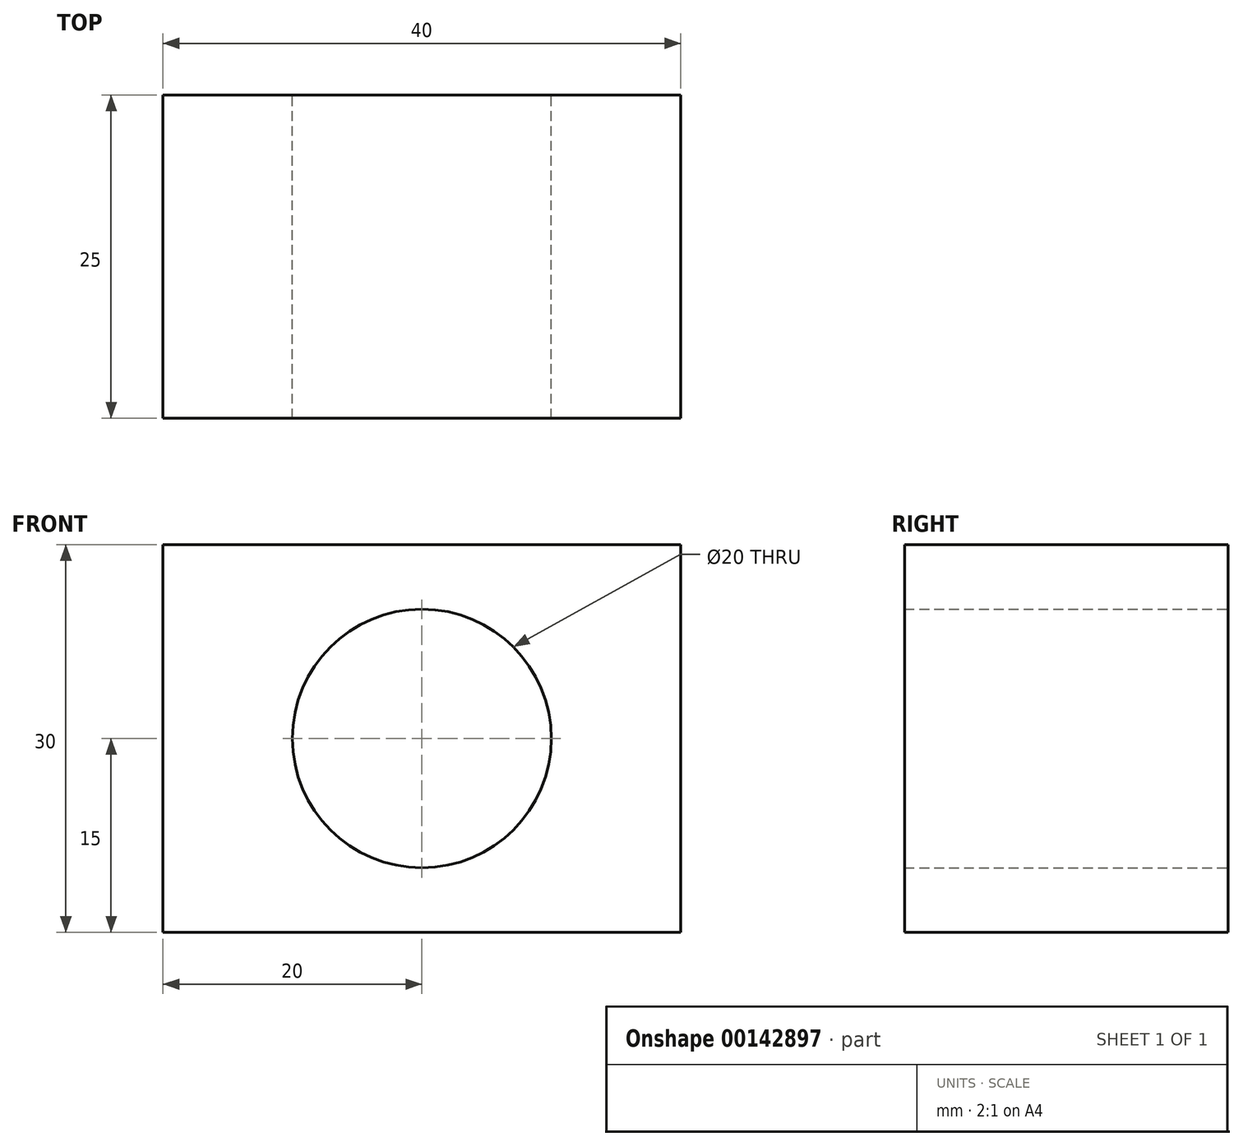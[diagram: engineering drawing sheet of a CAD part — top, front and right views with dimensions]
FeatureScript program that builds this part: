
annotation { "Feature Type Name" : "Feature", "Feature Type Description" : "" }
export const myFeature = defineFeature(function(context is Context, id is Id, definition is map)
    precondition{}
    {
        {
            var Q0;
            Q0=qCreatedBy(makeId("Front.planeOp"),FACE);
            var sketch = newSketch(context, id + "F0", { "sketchPlane" : qUnion([Q0])});
            skLineSegment(sketch, "E0.bottom", {"start": v(0, 0) * mm, "end": v(40, 0) * mm});
            skLineSegment(sketch, "E0.top", {"start": v(0, 30) * mm, "end": v(40, 30) * mm});
            skLineSegment(sketch, "E0.left", {"start": v(0, 0) * mm, "end": v(0, 30) * mm});
            skLineSegment(sketch, "E0.right", {"start": v(40, 0) * mm, "end": v(40, 30) * mm});
            skCircle(sketch, "E1", {"center": v(20, 15) * mm, "radius": 10 * mm});
            skPoint(sketch, "E1.centerSnap0", {"position": v(40, 15) * mm});
            skPoint(sketch, "E1.centerSnap1", {"position": v(20, 30) * mm});
            skSolve(sketch);
        }
        {
            var Q0;
            Q0 = qSketchRegion(id + "F0", true);
            extrude(context, id + "F1", {"entities" : qUnion([Q0]), "depth" : 25 * mm});
        }
    });
